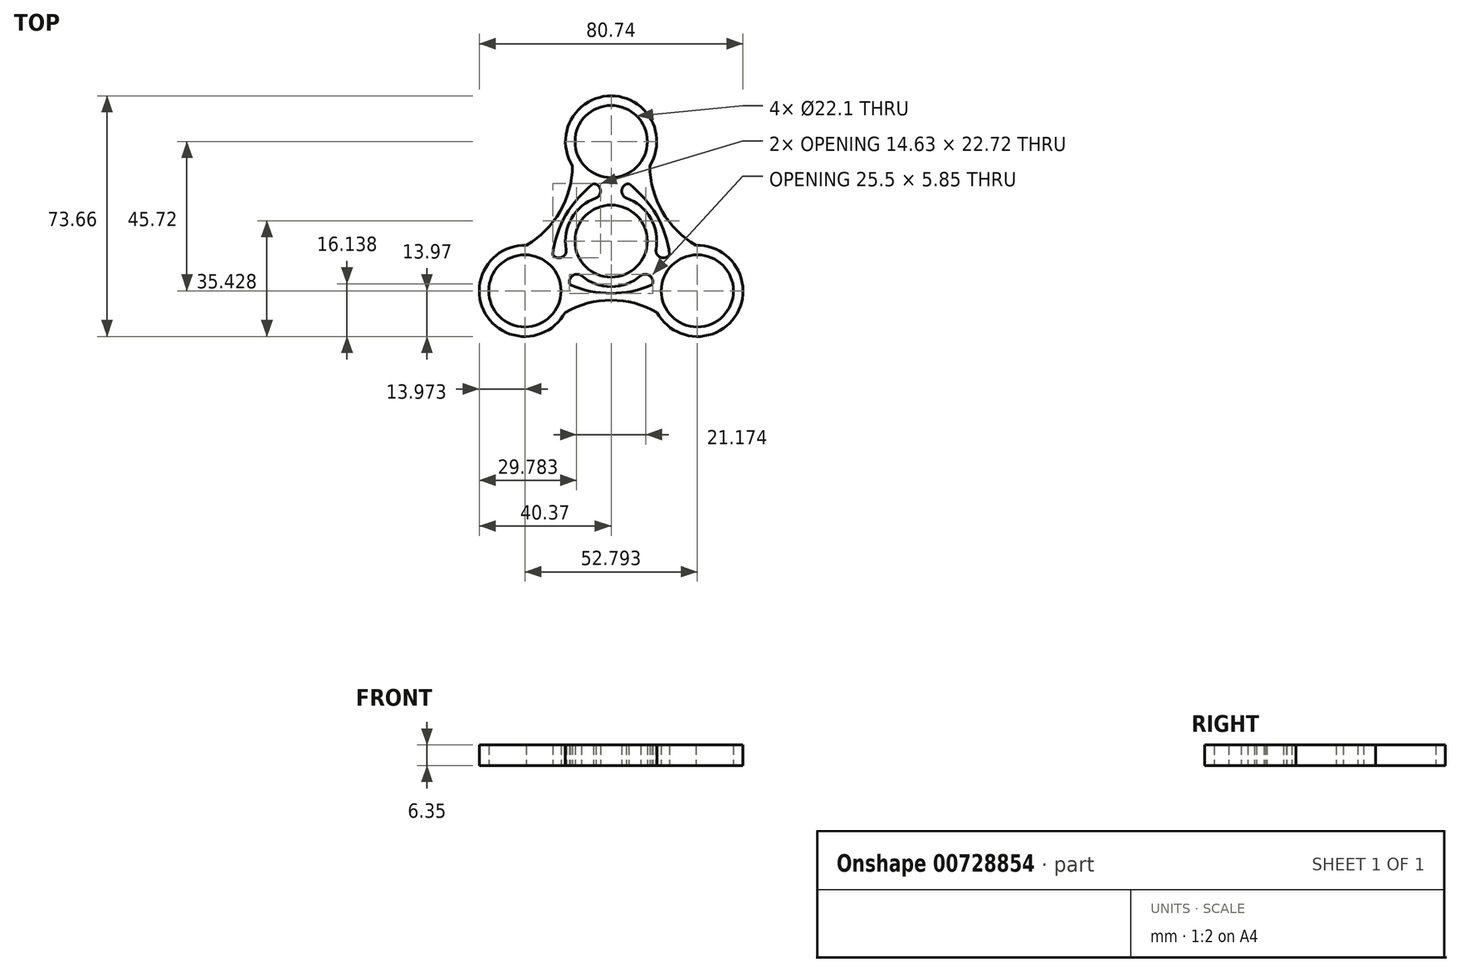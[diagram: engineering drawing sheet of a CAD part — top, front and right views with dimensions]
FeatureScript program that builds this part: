
annotation { "Feature Type Name" : "Feature", "Feature Type Description" : "" }
export const myFeature = defineFeature(function(context is Context, id is Id, definition is map)
    precondition{}
    {
        {
            var Q0;
            Q0=qCreatedBy(makeId("Top.planeOp"),FACE);
            var sketch = newSketch(context, id + "F0", { "sketchPlane" : qUnion([Q0])});
            skCircle(sketch, "E0", {"center": v(0, 0) * mm, "radius": 11.05 * mm});
            skArc(sketch, "E1", {"start": v(-4.61, 13.19) * mm, "mid": v(-12.1, 6.99) * mm, "end": v(-13.73, -2.6) * mm});
            skCircle(sketch, "E2", {"center": v(0, 30.48) * mm, "radius": 11.05 * mm});
            skArc(sketch, "E3", {"start": v(-5.35, 17.58) * mm, "mid": v(-4.79, 17.36) * mm, "end": v(-4.2, 17.16) * mm});
            skCircle(sketch, "E4.1.0", {"center": v(-26.4, -15.24) * mm, "radius": 11.05 * mm});
            skArc(sketch, "E4.1.1", {"start": v(-12.54, -13.43) * mm, "mid": v(-12.64, -12.82) * mm, "end": v(-12.76, -12.22) * mm});
            skCircle(sketch, "E4.2.0", {"center": v(26.4, -15.24) * mm, "radius": 11.05 * mm});
            skArc(sketch, "E4.2.1", {"start": v(17.9, -4.15) * mm, "mid": v(17.42, -4.53) * mm, "end": v(16.96, -4.93) * mm});
            skPoint(sketch, "E5.endSnap0", {"position": v(-14.42, 8.13) * mm});
            skArc(sketch, "E6.1.0", {"start": v(-12.54, -13.43) * mm, "mid": v(0, -16) * mm, "end": v(12.54, -13.43) * mm});
            skArc(sketch, "E6.1.1", {"start": v(14.08, -21.83) * mm, "mid": v(0, -18.07) * mm, "end": v(-14.08, -21.83) * mm});
            skPoint(sketch, "E7.MirrorCS.end.orphan", {"position": v(-7.21, 12.5) * mm});
            skPoint(sketch, "E7.MirrorCS.start.orphan", {"position": v(-5.35, 17.58) * mm});
            skPoint(sketch, "E6.2.2.end.orphan", {"position": v(7.21, 12.5) * mm});
            skPoint(sketch, "E5.end.orphan", {"position": v(-14.42, 0) * mm});
            skPoint(sketch, "E8.orphan", {"position": v(-17.9, -4.15) * mm});
            skPoint(sketch, "E6.2.0.end.orphan", {"position": v(5.35, 17.58) * mm});
            skArc(sketch, "E9.1.0", {"start": v(17.9, -4.15) * mm, "mid": v(13.85, 8) * mm, "end": v(5.35, 17.58) * mm});
            skArc(sketch, "E9.1.1", {"start": v(11.87, 23.1) * mm, "mid": v(15.65, 9.03) * mm, "end": v(25.94, -1.28) * mm});
            skArc(sketch, "E9.2.0", {"start": v(-5.35, 17.58) * mm, "mid": v(-13.85, 8) * mm, "end": v(-17.9, -4.15) * mm});
            skArc(sketch, "E9.2.1", {"start": v(-25.94, -1.28) * mm, "mid": v(-15.65, 9.03) * mm, "end": v(-11.87, 23.1) * mm});
            skArc(sketch, "E10", {"start": v(-4.61, 13.19) * mm, "mid": v(-3.28, 15.67) * mm, "end": v(-5.35, 17.58) * mm});
            skArc(sketch, "E11.MirrorCS", {"start": v(4.61, 13.19) * mm, "mid": v(3.28, 15.67) * mm, "end": v(5.35, 17.58) * mm});
            skArc(sketch, "E12.1.0", {"start": v(-9.11, -10.59) * mm, "mid": v(-11.93, -10.67) * mm, "end": v(-12.54, -13.43) * mm});
            skArc(sketch, "E12.1.1", {"start": v(-13.73, -2.6) * mm, "mid": v(-15.2, -5) * mm, "end": v(-17.9, -4.15) * mm});
            skArc(sketch, "E12.2.0", {"start": v(13.73, -2.6) * mm, "mid": v(15.2, -5) * mm, "end": v(17.9, -4.15) * mm});
            skArc(sketch, "E12.2.1", {"start": v(9.11, -10.59) * mm, "mid": v(11.93, -10.67) * mm, "end": v(12.54, -13.43) * mm});
            skArc(sketch, "E13.trimOffspring", {"start": v(-9.11, -10.59) * mm, "mid": v(0, -13.97) * mm, "end": v(9.11, -10.59) * mm});
            skArc(sketch, "E14.trimOffspring", {"start": v(13.73, -2.6) * mm, "mid": v(12.1, 6.98) * mm, "end": v(4.61, 13.19) * mm});
            skArc(sketch, "E15.trimOffspring", {"start": v(11.87, 23.1) * mm, "mid": v(0, 44.45) * mm, "end": v(-11.87, 23.1) * mm});
            skArc(sketch, "E16.trimOffspring", {"start": v(14.08, -21.83) * mm, "mid": v(38.5, -22.23) * mm, "end": v(25.94, -1.28) * mm});
            skArc(sketch, "E17.trimOffspring", {"start": v(-25.94, -1.28) * mm, "mid": v(-38.5, -22.22) * mm, "end": v(-14.08, -21.83) * mm});
            skArc(sketch, "E18.trimOffspring", {"start": v(-16.96, -4.93) * mm, "mid": v(-17.42, -4.53) * mm, "end": v(-17.9, -4.15) * mm});
            skArc(sketch, "E19.trimOffspring", {"start": v(4.2, 17.16) * mm, "mid": v(4.79, 17.36) * mm, "end": v(5.35, 17.58) * mm});
            skArc(sketch, "E20.trimOffspring", {"start": v(12.76, -12.22) * mm, "mid": v(12.64, -12.82) * mm, "end": v(12.54, -13.43) * mm});
            skSolve(sketch);
        }
        {
            var Q0;
            Q0 = qSketchRegion(id + "F0", true);
            extrude(context, id + "F1", {"entities" : qUnion([Q0]), "depth" : 6.35 * mm, "offsetDistance" : 25.4 * mm});
        }
    });
